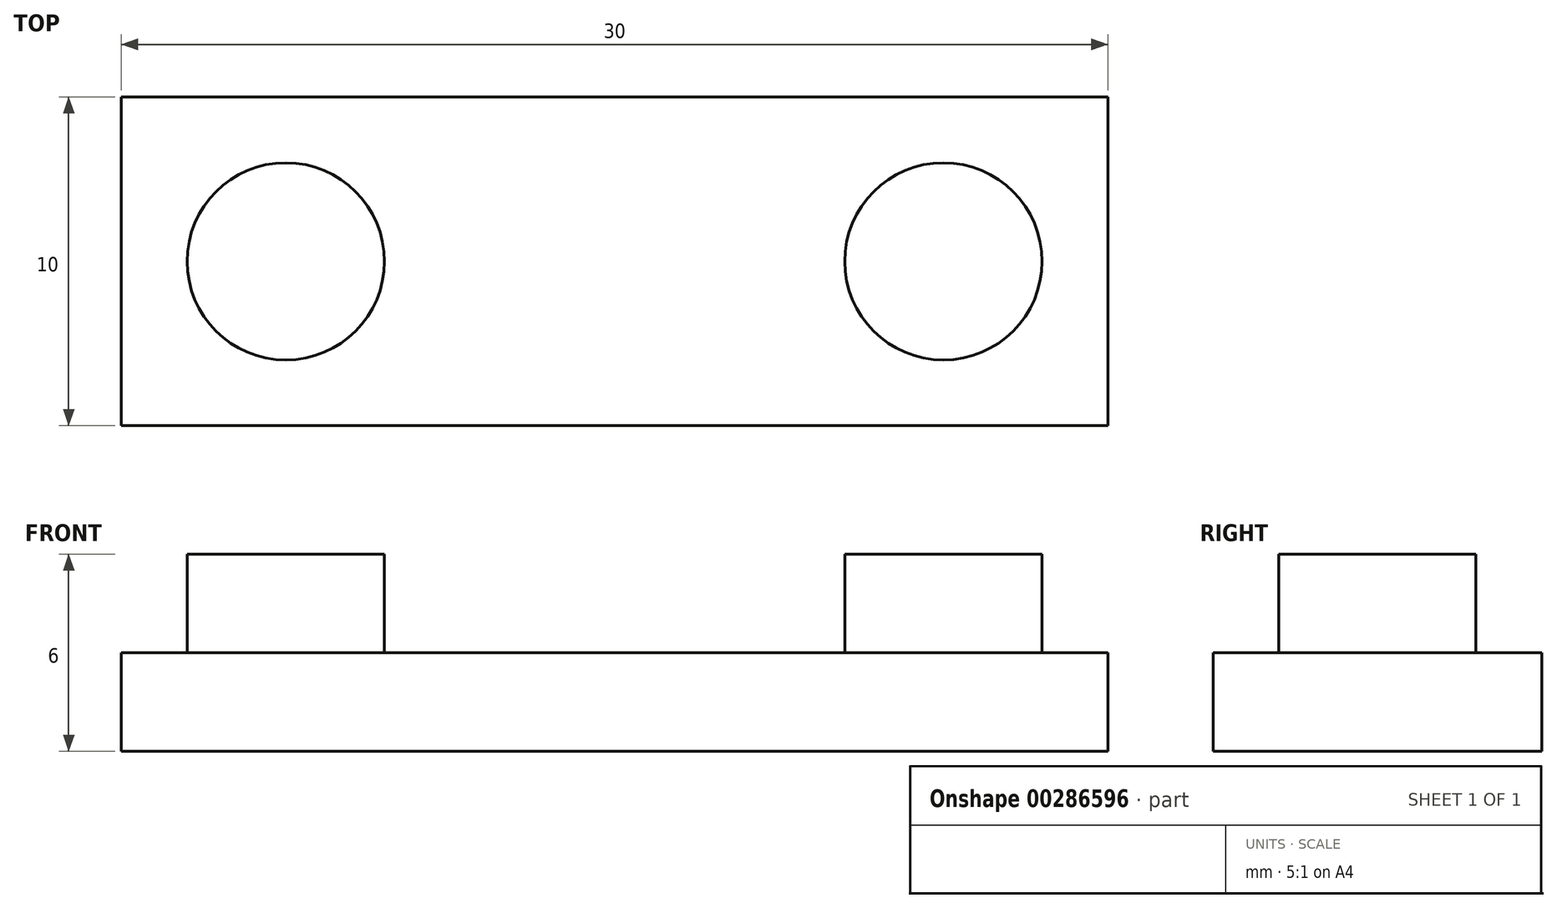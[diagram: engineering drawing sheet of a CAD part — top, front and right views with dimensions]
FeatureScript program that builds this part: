
annotation { "Feature Type Name" : "Feature", "Feature Type Description" : "" }
export const myFeature = defineFeature(function(context is Context, id is Id, definition is map)
    precondition{}
    {
        {
            var Q0;
            Q0=qCreatedBy(makeId("Top.planeOp"),FACE);
            var sketch = newSketch(context, id + "F0", { "sketchPlane" : qUnion([Q0])});
            skLineSegment(sketch, "E0.bottom", {"start": v(15, 5) * mm, "end": v(-15, 5) * mm});
            skLineSegment(sketch, "E0.top", {"start": v(15, -5) * mm, "end": v(-15, -5) * mm});
            skLineSegment(sketch, "E0.left", {"start": v(15, 5) * mm, "end": v(15, -5) * mm});
            skLineSegment(sketch, "E0.right", {"start": v(-15, 5) * mm, "end": v(-15, -5) * mm});
            skPoint(sketch, "E0.middle", {"position": v(0, 0) * mm});
            skCircle(sketch, "E1", {"center": v(-10, 0) * mm, "radius": 3 * mm});
            skCircle(sketch, "E2", {"center": v(10, 0) * mm, "radius": 3 * mm});
            skSolve(sketch);
        }
        {
            var Q0;
            Q0=makeQuery(id+"F0.imprint","IMPRINT",FACE,{"disambiguationData":[TD([[makeQuery(id+"F0.imprint","IMPRINT",EDGE,{"derivedFrom":sQuery(id+"F0.wireOp",EDGE,"E0.bottom")}),1.0]])]});
            var Q1;
            Q1=makeQuery(id+"F0.imprint","IMPRINT",FACE,{"disambiguationData":[TD([[makeQuery(id+"F0.imprint","IMPRINT",EDGE,{"derivedFrom":sQuery(id+"F0.wireOp",EDGE,"E2")}),1.0]])]});
            var Q2;
            Q2=makeQuery(id+"F0.imprint","IMPRINT",FACE,{"disambiguationData":[TD([[makeQuery(id+"F0.imprint","IMPRINT",EDGE,{"derivedFrom":sQuery(id+"F0.wireOp",EDGE,"E1")}),1.0]])]});
            extrude(context, id + "F1", {"entities" : qUnion([Q0, Q1, Q2]), "depth" : 3 * mm});
        }
        {
            var Q0;
            Q0=makeQuery(id+"F0.imprint","IMPRINT",FACE,{"disambiguationData":[TD([[makeQuery(id+"F0.imprint","IMPRINT",EDGE,{"derivedFrom":sQuery(id+"F0.wireOp",EDGE,"E1")}),1.0]])]});
            var Q1;
            Q1=makeQuery(id+"F0.imprint","IMPRINT",FACE,{"disambiguationData":[TD([[makeQuery(id+"F0.imprint","IMPRINT",EDGE,{"derivedFrom":sQuery(id+"F0.wireOp",EDGE,"E2")}),1.0]])]});
            extrude(context, id + "F2", {"entities" : qUnion([Q0, Q1]), "operationType" : NewBodyOperationType.ADD, "depth" : 6 * mm});
        }
    });
